# Revit family: QF_ELECTROLUXPROFESSIONAL_1LSNTR_WN6-35_E
name_source: partatom
category: Attrezzature speciali
units: mm (PartAtom-declared; Revit-internal decimal feet)

## family parameters
Basato su piano di lavoro = No
Condiviso = No
Punto di calcolo locali = No
Quota connettore circolare = Usa diametro
Sempre verticale = Sì
Taglio con vuoti quando caricato = No
Tipo di parte = Normale

## types (16) — shared parameters
Depth = 1115.4 mm  [stored 3.65945 ft]
Depth Actual = 1115 mm  [stored 3.65814 ft]
Height = 1466.8 mm  [stored 4.81234 ft]
Height Actual = 1465 mm  [stored 4.80643 ft]
Latent Heat Output = 0.0
Length Actual = 910 mm  [stored 2.98556 ft]
Modello = WN6-35
Produttore = Electrolux Professional
Sensible Heat Output = 0.0
URL = www.electroluxprofessional.com
Weight = 307
Width = 910 mm  [stored 2.98556 ft]
zero-valued in all types: Gas KW, Prospetto di default, Steam Pounds per Hour

## per-type parameters (varying)
| type | Cycle | Descrizione | Item Number | Phase | Volts | Watts |
| 9868130093 | 50 Hz | WASHER WN6-35 35KG EL 19,8KW 415/50/3N COMPASS PRO 6H12 ML 2xWATER POWDER+5xLIQ. VALV.CLOSED SILVER 2.I/O DISCON. STOP H | 1L0G8W | 3 | 415 V | 20900 W |
| 9868130294 | 50 Hz | WASHER WN6-35 35KG EL 19,1KW 380-400/50/3N COMPASS PRO 6G01 ML 2xWATER POWDER VALV.CLOSED SILVER DISCON. STOP | 1L0H04 | 3 | 400 V | 20200 W |
| 9868130257 | 60 Hz | WASHER WN6-35 35KG NO HEAT 440/60/1 COMPASS PRO 6G07 ML 2xWATER POWDER+5xLIQ. VALV.OPEN SILVER 2.I/O TRAFO DISCON. STOP | 1LSPEJ | 1 | 440 V | 1300 W |
| 9868130331 | 50 Hz | WASHER WN6-35 35KG NO HEAT 220-240/50/1N COMPASS PRO 6L01 ML 2xWATER 5xLIQ. VALV.OPEN SST/SILVER EXT.PM. 2.I/O DISCON. | 1L0H8F | 1 | 240 V | 1300 W |
| 9868130233 | 60 Hz | WASHER WN6-35 35KG NO HEAT 220-240/60/1N COMPASS PRO 6G01 ML 2xWATER POWDER+5xLIQ. VALV.OPEN SILVER 2.I/O QC DISCON. STO | 1LA22H | 1 | 240 V | 1300 W |
| 9868130276 | 60 Hz | WASHER WN6-35 35KG EL 19,8KW 240/60/3 COMPASS PRO 6G07 ML 2xWATER POWDER+5xLIQ. VALV.OPEN SST/SILVER 2.I/O DISCON. STOP | 1L0GWE | 3 | 240 V | 20900 W |
| 9868130178 | 50 Hz | WASHER WN6-35 35KG NO HEAT 220-240/50/1N COMPASS PRO 6G01 ML 2xWATER POWDER VALV.OPEN SILVER DISCON. STOP | 1L0GCH | 1 | 240 V | 1300 W |
| 9868130326 | 60 Hz | WASHER WN6-35 35KG EL 22,8KW 480/60/3 COMPASS PRO 6G07 ML 2xWATER POWDER+5xLIQ. VALV.OPEN SILVER 2.I/O TRAFO DISCON. STO | 1L0H5V | 3 | 480 V | 24100 W |
| 9868130290 | 50 Hz | WASHER WN6-35 35KG EL 19,1KW 380-400/50/3N COMPASS PRO 6G01 ML 2xWATER POWDER+5xLIQ. VALV.OPEN SST 2.I/O DISCON. STOP | 1L828A | 3 | 400 V | 20200 W |
| 9868130255 | 60 Hz | WASHER WN6-35 35KG EL 21KW 440/60/3 COMPASS PRO 6G07 ML 2xWATER POWDER+5xLIQ. VALV.OPEN SILVER 2.I/O TRAFO DISCON. STOP | 1L0GSK | 3 | 440 V | 22200 W |
| 9868130192 | 50 Hz | WASHER WN6-35 35KG EL 19,1KW 380-400/50/3N COMPASS PRO 6H12 ML 2xWATER POWDER+5xLIQ. VALV.OPEN SILVER SL.DRUM 2.I/O DISC | 1LA1CX | 3 | 400 V | 20200 W |
| 9868130179 | 50 Hz | WASHER WN6-35 35KG EL 19,1KW 380-400/50/3N COMPASS PRO 6G01 ML 2xWATER POWDER+5xLIQ. VALV.OPEN SILVER 2.I/O DISCON. STOP | 1L0GCY | 3 | 400 V | 20200 W |
| 9868130297 | 60 Hz | WASHER WN6-35 35KG EL 19,1KW 380-400/60/3N COMPASS PRO 6G01 ML 2xWATER POWDER+5xLIQ. VALV.OPEN SILVER 2.I/O DISCON. STOP | 1LSPND | 3 | 400 V | 20200 W |
| 9868130137 | 50 Hz | WASHER WN6-35 35KG EL 19,1KW 380-400/50/3N COMPASS PRO 6G01 ML 2xWATER POWDER VALV.OPEN SILVER DISCON. STOP | 1L8246 | 3 | 400 V | 20200 W |
| 9868130201 | 50 Hz | WASHER WN6-35 35KG EL 19,8KW 415/50/3N COMPASS PRO 6H01 ML 2xWATER POWDER+5xLIQ. VALV.OPEN SST/SILVER 2.I/O DISCON. STOP | 1L0GDL | 3 | 415 V | 20900 W |
| 9868130193 | 50 Hz | WASHER WN6-35 35KG EL 19,8KW 415/50/3N COMPASS PRO 6H12 ML 2xWATER POWDER+5xLIQ. VALV.CLOSED SST/SILVER SL.DRUM 2.I/O DI | 1LA1D9 | 3 | 415 V | 20900 W |

note: [stored X ft] marks values corroborated as IEEE doubles in the binary element streams (Revit-internal decimal feet)

## geometry (parser evidence)
native form markers: Sweep x5
no freeform markers — native parametric forms only
